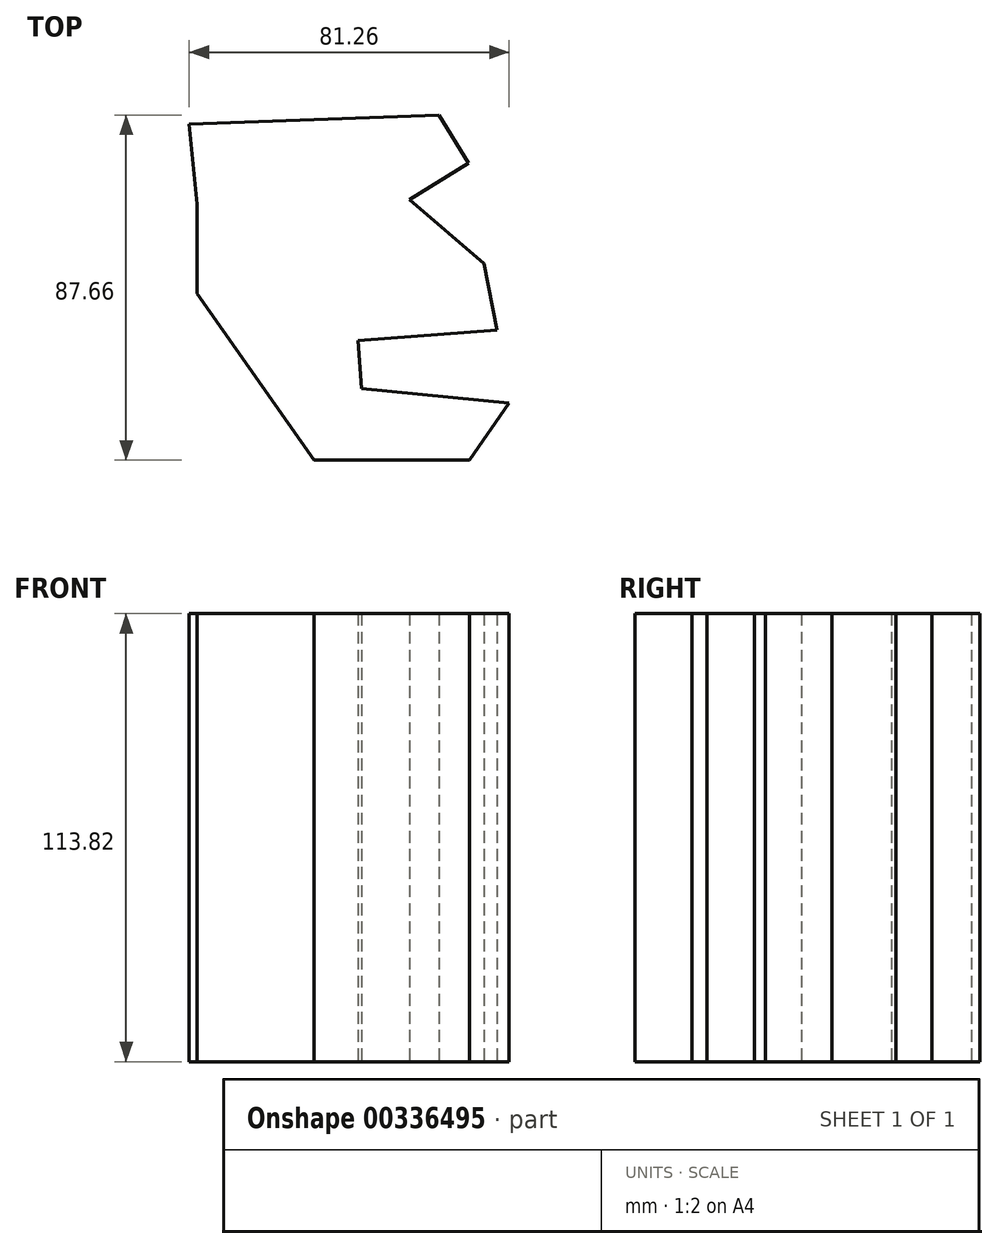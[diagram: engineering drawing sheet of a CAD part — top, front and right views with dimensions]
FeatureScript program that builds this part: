
annotation { "Feature Type Name" : "Feature", "Feature Type Description" : "" }
export const myFeature = defineFeature(function(context is Context, id is Id, definition is map)
    precondition{}
    {
        {
            var Q0;
            Q0=qCreatedBy(makeId("Top.planeOp"),FACE);
            var sketch = newSketch(context, id + "F0", { "sketchPlane" : qUnion([Q0])});
            skLineSegment(sketch, "E0", {"start": v(-42.86, 35.48) * mm, "end": v(20.6, 37.7) * mm});
            skLineSegment(sketch, "E1", {"start": v(20.6, 37.7) * mm, "end": v(28.1, 25.46) * mm});
            skLineSegment(sketch, "E2", {"start": v(28.1, 25.46) * mm, "end": v(13.14, 16.28) * mm});
            skLineSegment(sketch, "E3", {"start": v(13.14, 16.28) * mm, "end": v(32, 0) * mm});
            skLineSegment(sketch, "E4", {"start": v(32, 0) * mm, "end": v(35.34, -16.84) * mm});
            skLineSegment(sketch, "E5", {"start": v(35.34, -16.84) * mm, "end": v(0, -19.62) * mm});
            skLineSegment(sketch, "E6", {"start": v(0, -19.62) * mm, "end": v(0.95, -31.72) * mm});
            skLineSegment(sketch, "E7", {"start": v(0.95, -31.72) * mm, "end": v(38.4, -35.48) * mm});
            skLineSegment(sketch, "E8", {"start": v(38.4, -35.48) * mm, "end": v(28.39, -49.95) * mm});
            skLineSegment(sketch, "E9", {"start": v(28.39, -49.95) * mm, "end": v(-11.13, -49.95) * mm});
            skLineSegment(sketch, "E10", {"start": v(-11.13, -49.95) * mm, "end": v(-40.9, -7.65) * mm});
            skLineSegment(sketch, "E11", {"start": v(-40.9, -7.65) * mm, "end": v(-40.9, 15.17) * mm});
            skLineSegment(sketch, "E12", {"start": v(-40.9, 15.17) * mm, "end": v(-42.86, 35.48) * mm});
            skSolve(sketch);
        }
        {
            var Q0;
            Q0=makeQuery(id+"F0.imprint","IMPRINT",FACE,{"disambiguationData":[TD([[makeQuery(id+"F0.imprint","IMPRINT",EDGE,{"derivedFrom":sQuery(id+"F0.wireOp",EDGE,"E0")}),-1.0]])]});
            extrude(context, id + "F1", {"entities" : qUnion([Q0]), "endBound" : BoundingType.SYMMETRIC, "depth" : 30 * mm});
        }
        {
            var Q0;
            Q0=makeQuery(id+"F1.opExtrude","CAP_FACE",FACE,{"disambiguationData":[OSD([sQuery(id+"F0.wireOp",EDGE,"E0"),sQuery(id+"F0.wireOp",EDGE,"E1"),sQuery(id+"F0.wireOp",EDGE,"E2"),sQuery(id+"F0.wireOp",EDGE,"E3"),sQuery(id+"F0.wireOp",EDGE,"E4"),sQuery(id+"F0.wireOp",EDGE,"E5"),sQuery(id+"F0.wireOp",EDGE,"E6"),sQuery(id+"F0.wireOp",EDGE,"E7"),sQuery(id+"F0.wireOp",EDGE,"E8"),sQuery(id+"F0.wireOp",EDGE,"E9"),sQuery(id+"F0.wireOp",EDGE,"E10"),sQuery(id+"F0.wireOp",EDGE,"E11"),sQuery(id+"F0.wireOp",EDGE,"E12")])],"isStart":false});
            extrude(context, id + "F2", {"entities" : qUnion([Q0]), "operationType" : NewBodyOperationType.ADD, "depth" : 83.82 * mm});
        }
    });
